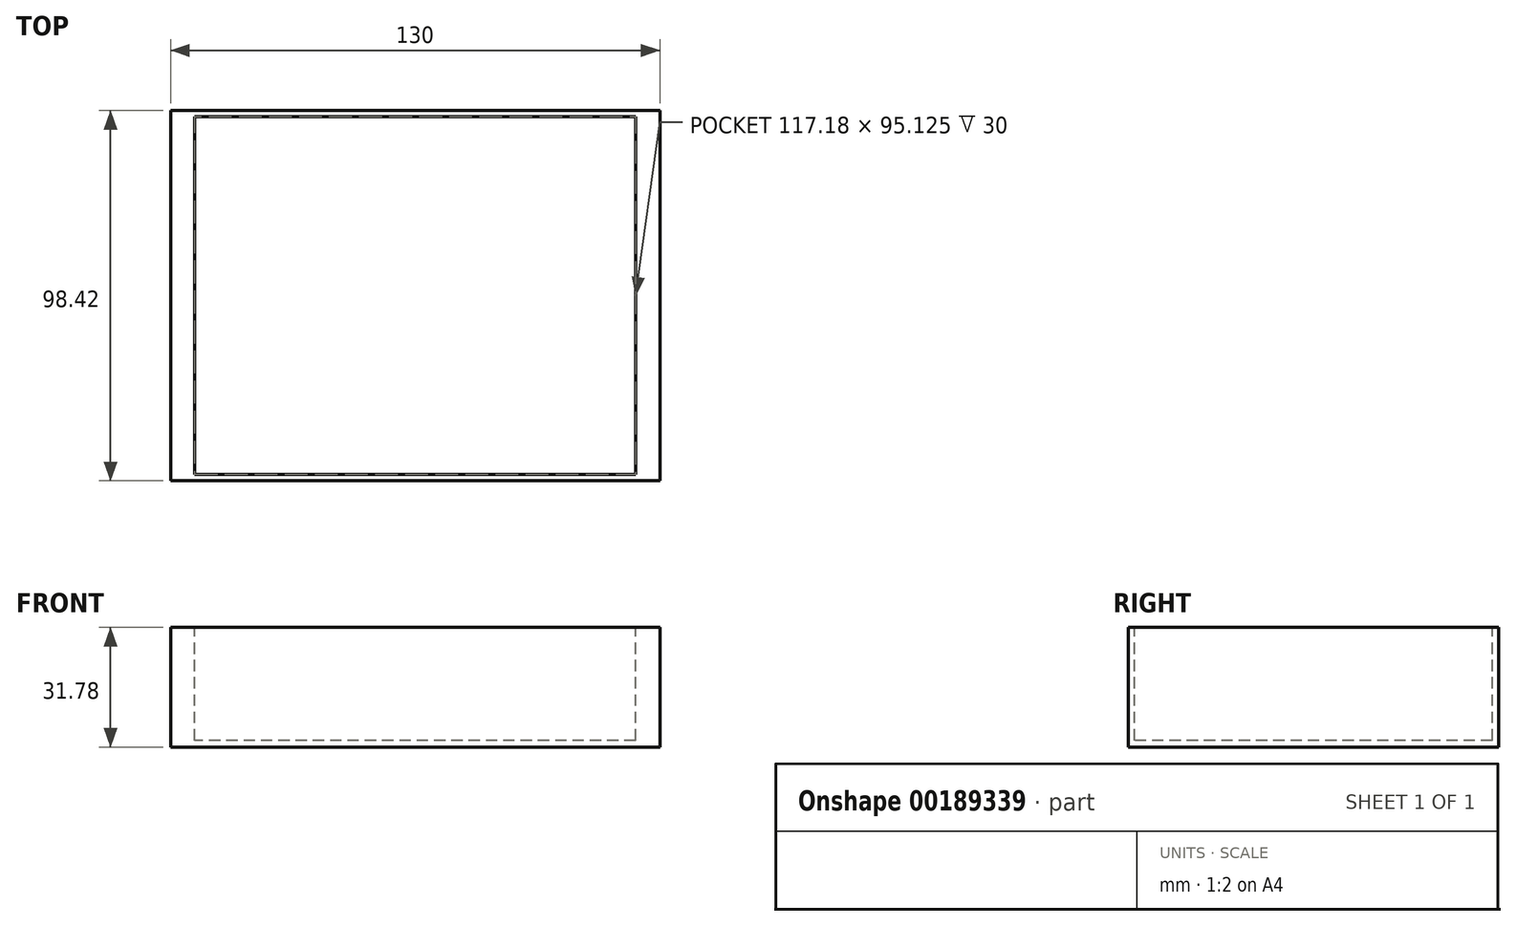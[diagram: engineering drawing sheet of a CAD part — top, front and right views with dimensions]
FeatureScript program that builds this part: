
annotation { "Feature Type Name" : "Feature", "Feature Type Description" : "" }
export const myFeature = defineFeature(function(context is Context, id is Id, definition is map)
    precondition{}
    {
        {
            var Q0;
            Q0=qCreatedBy(makeId("Top.planeOp"),FACE);
            var sketch = newSketch(context, id + "F0", { "sketchPlane" : qUnion([Q0])});
            skLineSegment(sketch, "E0.bottom", {"start": v(65, -49.21) * mm, "end": v(-65, -49.21) * mm});
            skLineSegment(sketch, "E0.top", {"start": v(65, 49.21) * mm, "end": v(-65, 49.21) * mm});
            skLineSegment(sketch, "E0.left", {"start": v(65, -49.21) * mm, "end": v(65, 49.21) * mm});
            skLineSegment(sketch, "E0.right", {"start": v(-65, -49.21) * mm, "end": v(-65, 49.21) * mm});
            skPoint(sketch, "E0.middle", {"position": v(0, 0) * mm});
            skSolve(sketch);
        }
        {
            var Q0;
            Q0=makeQuery(id+"F0.imprint","IMPRINT",FACE,{"disambiguationData":[TD([[makeQuery(id+"F0.imprint","IMPRINT",EDGE,{"derivedFrom":sQuery(id+"F0.wireOp",EDGE,"E0.bottom")}),-1.0]])]});
            extrude(context, id + "F1", {"entities" : qUnion([Q0]), "depth" : 31.78 * mm});
        }
        {
            var Q0;
            Q0=makeQuery(id+"F1.opExtrude","CAP_FACE",FACE,{"disambiguationData":[OSD([sQuery(id+"F0.wireOp",EDGE,"E0.bottom"),sQuery(id+"F0.wireOp",EDGE,"E0.top"),sQuery(id+"F0.wireOp",EDGE,"E0.left"),sQuery(id+"F0.wireOp",EDGE,"E0.right")])],"isStart":false});
            var sketch = newSketch(context, id + "F2", { "sketchPlane" : qUnion([Q0])});
            skLineSegment(sketch, "E1.bottom", {"start": v(58.6, 47.56) * mm, "end": v(-58.6, 47.56) * mm});
            skLineSegment(sketch, "E1.top", {"start": v(58.6, -47.56) * mm, "end": v(-58.6, -47.56) * mm});
            skLineSegment(sketch, "E1.left", {"start": v(58.6, 47.56) * mm, "end": v(58.6, -47.56) * mm});
            skLineSegment(sketch, "E1.right", {"start": v(-58.6, 47.56) * mm, "end": v(-58.6, -47.56) * mm});
            skPoint(sketch, "E1.middle", {"position": v(0, 0) * mm});
            skSolve(sketch);
        }
        {
            var Q0;
            Q0 = qSketchRegion(id + "F2", true);
            extrude(context, id + "F3", {"entities" : qUnion([Q0]), "operationType" : NewBodyOperationType.REMOVE, "oppositeDirection" : true, "depth" : 30 * mm});
        }
    });
